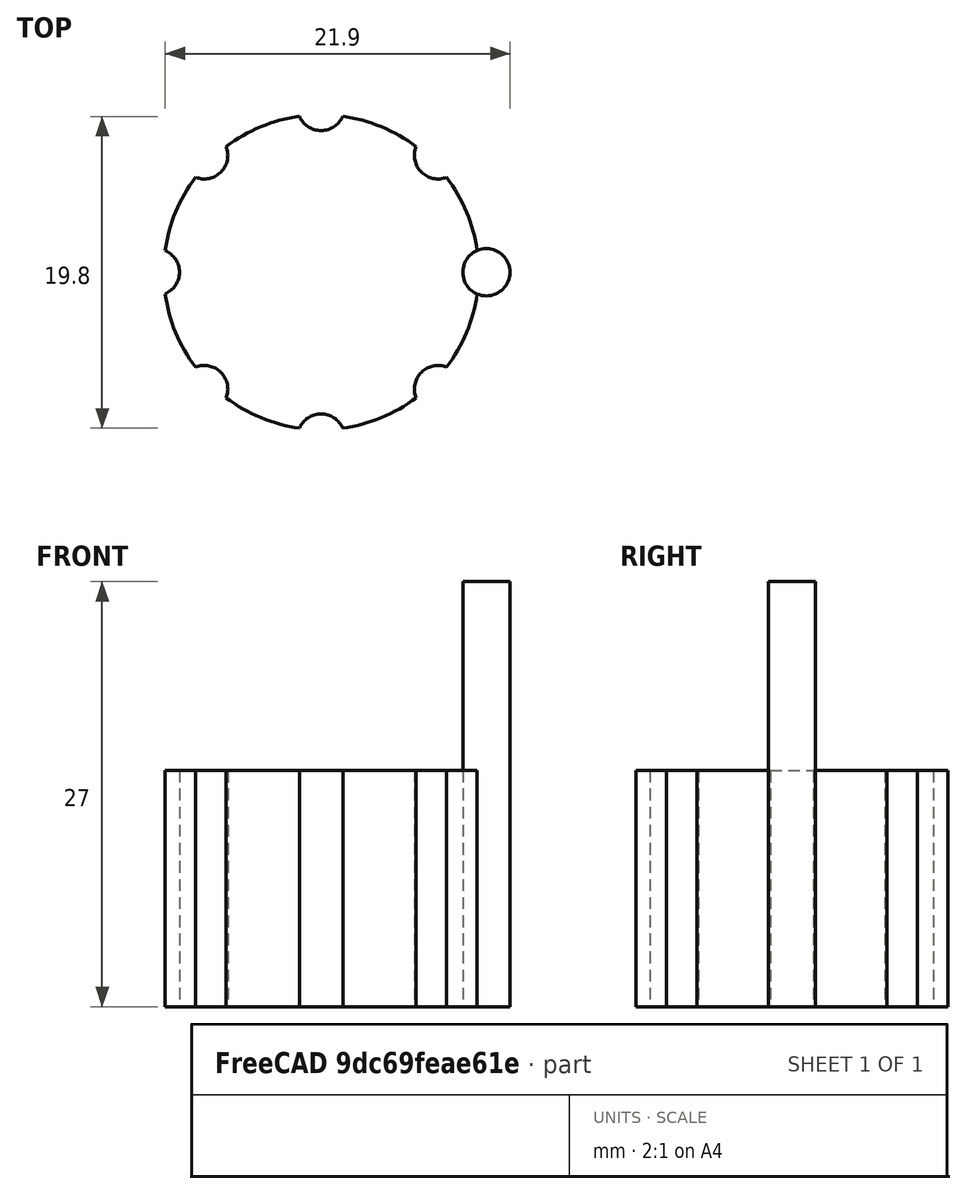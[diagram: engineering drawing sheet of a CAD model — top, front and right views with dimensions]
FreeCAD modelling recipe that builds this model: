
FCSTD DOCUMENT  (FreeCAD 1.0R39319 (Git))
Label: ojt1_t11r01_button
License: All rights reserved
LicenseURL: https://en.wikipedia.org/wiki/All_rights_reserved
objects: Part::Cylinder×2, Part::FeaturePython×1, Part::Cut×1
note: 3 computed .brp shape members not serialized (recipe doc carries the construction recipe); baked Part::Feature solids carry a one-line shape summary decoded from their .brp

FEATURE [Part::Cylinder] Cylinder
  Angle = 360
  AttacherType = Attacher::AttachEngine3D
  FirstAngle = 0
  Height = 15
  Radius = 10
  SecondAngle = 0
FEATURE [Part::Cylinder] Cylinder001
  Angle = 360
  AttacherType = Attacher::AttachEngine3D
  FirstAngle = 0
  Height = 27
  Placement = pos=(10.5,0,0) rot=(0,0,1;0rad)
  Radius = 1.5
  SecondAngle = 0
FEATURE [Part::FeaturePython] Array  # Draft array (typed FeaturePython)
  AlwaysSyncPlacement = false
  Angle = 360
  ArrayType = 1
  Axis = (0,0,0)
  Base = -> Cylinder001
  Center = (0,0,0)
  Count = 8
  ExpandArray = false
  Fuse = false
  IntervalAxis = (0,0,0)
  IntervalX = (50,0,0)
  IntervalY = (0,50,0)
  IntervalZ = (0,0,50)
  NumberCircles = 3
  NumberPolar = 8
  NumberX = 2
  NumberY = 2
  NumberZ = 1
  PlacementList = 8 placements: [(10.5,0,0),(7.42462,7.42462,0),(0,10.5,0),(-7.42462,7.42462,0),(-10.5,1.28588e-15,0),(-7.42462,-7.42462,0),(-2.33147e-15,-10.5,0),(7.42462,-7.42462,0)]
  RadialDistance = 50
  ScaleList = (8) [(1,1,1),(1,1,1),(1,1,1),(1,1,1),(1,1,1),(1,1,1),(1,1,1),(1,1,1)]
  Symmetry = 1
  TangentialDistance = 25
FEATURE [Part::Cut] Cut
  Base = -> Cylinder
  Refine = true
  Tool = -> Array
